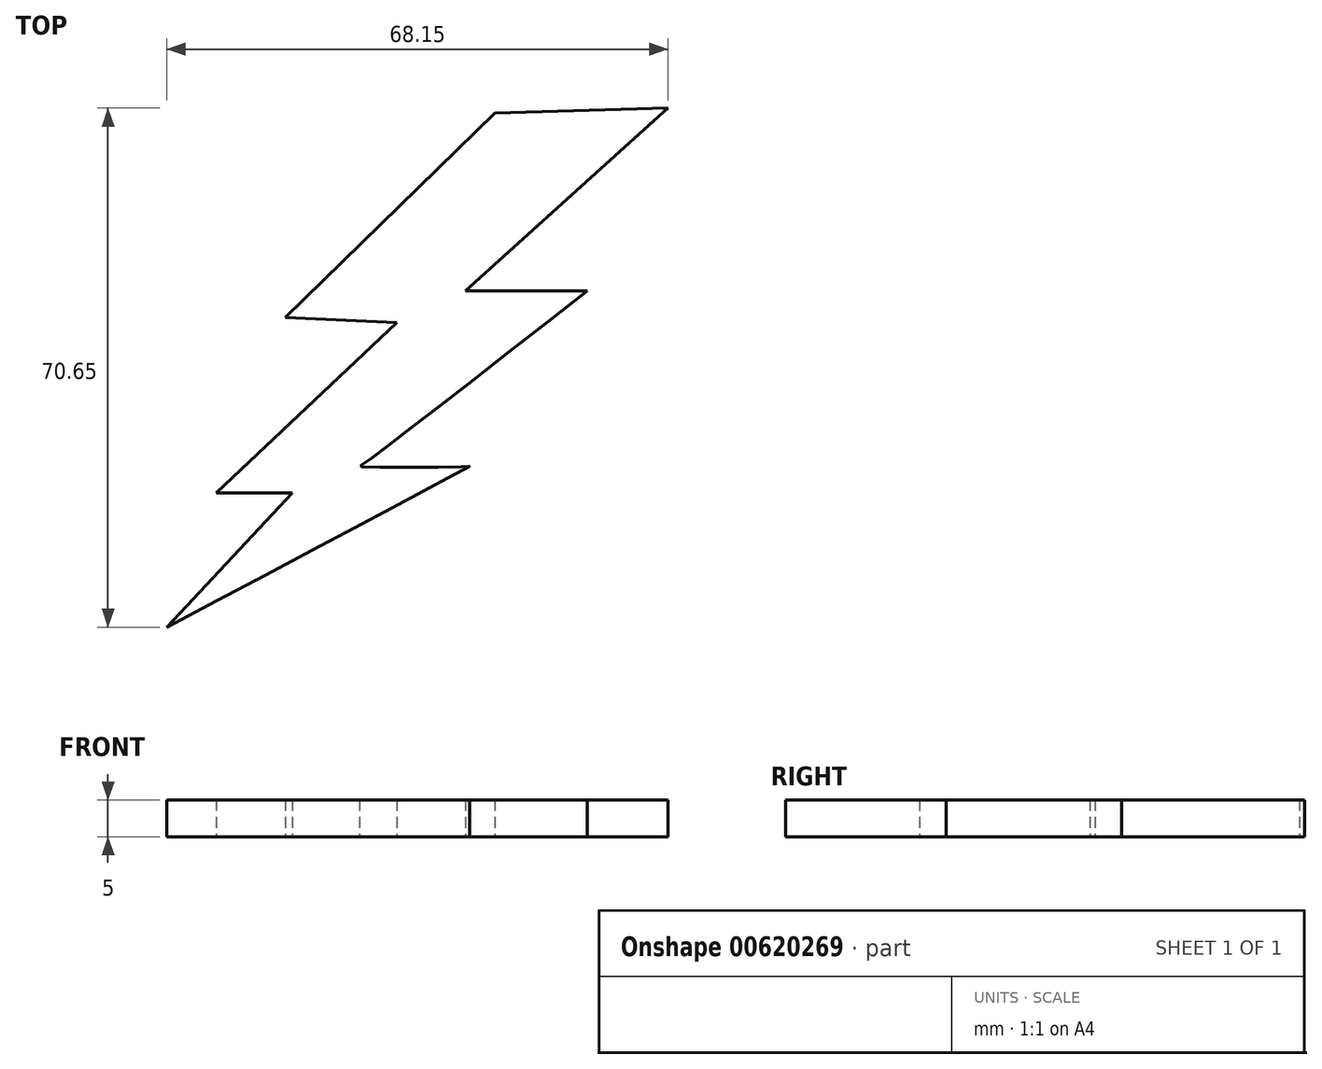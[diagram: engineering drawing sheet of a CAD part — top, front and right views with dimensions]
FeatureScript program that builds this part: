
annotation { "Feature Type Name" : "Feature", "Feature Type Description" : "" }
export const myFeature = defineFeature(function(context is Context, id is Id, definition is map)
    precondition{}
    {
        {
            var Q0;
            Q0=qCreatedBy(makeId("Top.planeOp"),FACE);
            var sketch = newSketch(context, id + "F0", { "sketchPlane" : qUnion([Q0])});
            skFitSpline(sketch, "E0", {"points": [v(-68.74, 0.96) * mm, v(-27.58, 22.83) * mm, v(-27.65, 22.83) * mm, v(-42.54, 22.8) * mm, v(-42.46, 22.87) * mm, v(-11.56, 46.72) * mm], "startDerivative": vector(156.9, 83.06) * mm, "endDerivative": vector(123.73, 96.73) * mm});
            skFitSpline(sketch, "E1", {"points": [v(-11.56, 46.72) * mm, v(-28.12, 46.72) * mm], "startDerivative": vector(-16.56, 0) * mm, "endDerivative": vector(-16.56, 0) * mm});
            skFitSpline(sketch, "E2", {"points": [v(-28.12, 46.72) * mm, v(-0.59, 71.6) * mm], "startDerivative": vector(27.53, 24.88) * mm, "endDerivative": vector(27.53, 24.88) * mm});
            skFitSpline(sketch, "E3", {"points": [v(-0.59, 71.6) * mm, v(-24.14, 70.93) * mm], "startDerivative": vector(-23.56, -0.68) * mm, "endDerivative": vector(-23.56, -0.68) * mm});
            skFitSpline(sketch, "E4", {"points": [v(-24.14, 70.93) * mm, v(-52.66, 43.1) * mm], "startDerivative": vector(-28.51, -27.83) * mm, "endDerivative": vector(-28.51, -27.83) * mm});
            skFitSpline(sketch, "E5", {"points": [v(-52.66, 43.1) * mm, v(-37.47, 42.42) * mm], "startDerivative": vector(15.18, -0.68) * mm, "endDerivative": vector(15.18, -0.68) * mm});
            skFitSpline(sketch, "E6", {"points": [v(-37.47, 42.42) * mm, v(-62.03, 19.23) * mm], "startDerivative": vector(-24.55, -23.2) * mm, "endDerivative": vector(-24.55, -23.2) * mm});
            skFitSpline(sketch, "E7", {"points": [v(-62.03, 19.23) * mm, v(-51.66, 19.23) * mm], "startDerivative": vector(10.37, 0) * mm, "endDerivative": vector(10.37, 0) * mm});
            skFitSpline(sketch, "E8", {"points": [v(-51.66, 19.23) * mm, v(-68.74, 0.96) * mm], "startDerivative": vector(-17.08, -18.26) * mm, "endDerivative": vector(-17.08, -18.26) * mm});
            skSolve(sketch);
        }
        {
            var Q0;
            Q0=makeQuery(id+"F0.imprint","IMPRINT",FACE,{"disambiguationData":[TD([[makeQuery(id+"F0.imprint","IMPRINT",EDGE,{"derivedFrom":sQuery(id+"F0.wireOp",EDGE,"E0")}),1.0]])]});
            extrude(context, id + "F1", {"entities" : qUnion([Q0]), "depth" : 5 * mm, "offsetDistance" : 25 * mm});
        }
    });
